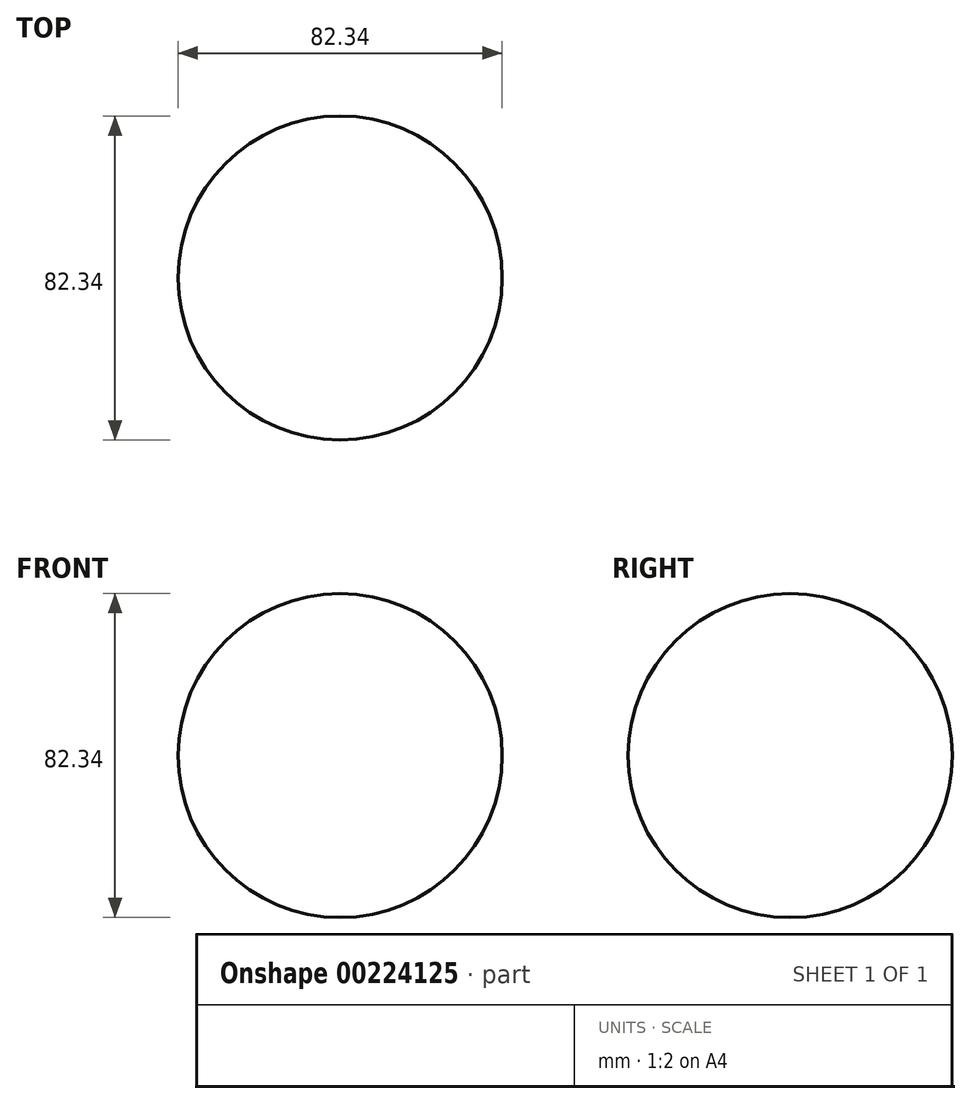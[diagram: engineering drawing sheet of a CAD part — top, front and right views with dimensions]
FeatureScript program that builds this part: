
annotation { "Feature Type Name" : "Feature", "Feature Type Description" : "" }
export const myFeature = defineFeature(function(context is Context, id is Id, definition is map)
    precondition{}
    {
        {
            var Q0;
            Q0=qCreatedBy(makeId("Front.planeOp"),FACE);
            var sketch = newSketch(context, id + "F0", { "sketchPlane" : qUnion([Q0])});
            skCircle(sketch, "E0", {"center": v(0, 0) * mm, "radius": 41.17 * mm});
            skLineSegment(sketch, "E1", {"start": v(0, 41.17) * mm, "end": v(0, -41.17) * mm});
            skSolve(sketch);
        }
        {
            var Q0;
            {var subQ0=sQuery(id+"F0.wireOp",EDGE,"E1");Q0=makeQuery(id+"F0.imprint","IMPRINT",FACE,{"disambiguationData":[TD([[makeQuery(id+"F0.imprint","IMPRINT",EDGE,{"derivedFrom":subQ0}),1.0]])]});}
            var Q1;
            Q1=sQuery(id+"F0.wireOp",EDGE,"E1");
            revolve(context, id + "F1", {"entities" : qUnion([Q0]), "axis" : qUnion([Q1]), "revolveType" : RevolveType.FULL});
        }
    });
